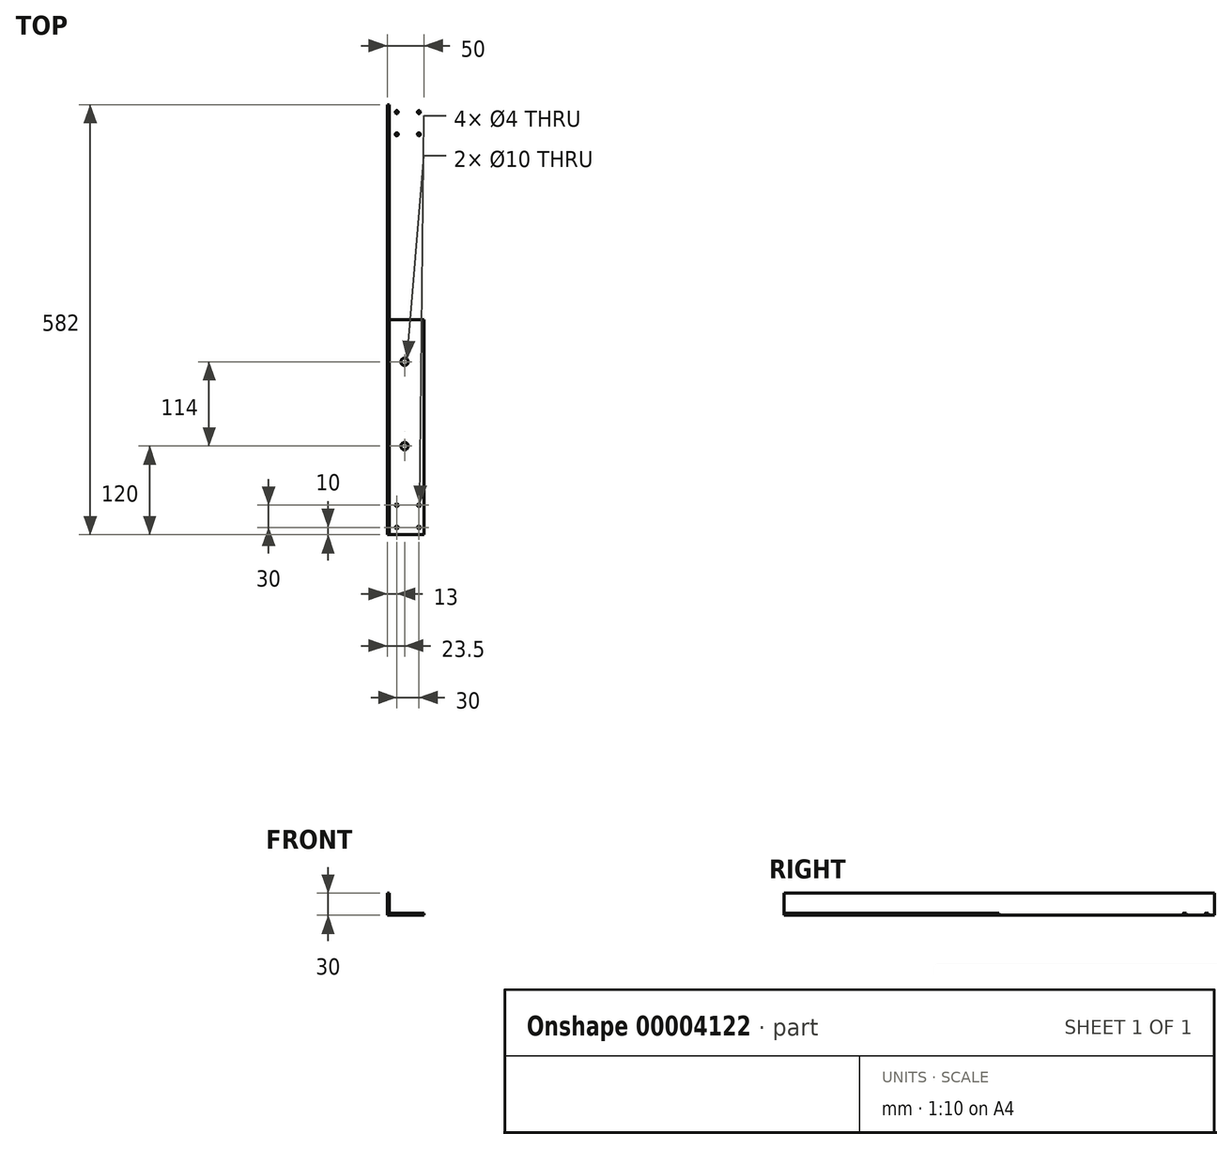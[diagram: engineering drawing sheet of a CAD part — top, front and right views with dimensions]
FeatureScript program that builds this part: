
annotation { "Feature Type Name" : "Feature", "Feature Type Description" : "" }
export const myFeature = defineFeature(function(context is Context, id is Id, definition is map)
    precondition{}
    {
        {
            var Q0;
            Q0=qCreatedBy(makeId("Front.planeOp"),FACE);
            var sketch = newSketch(context, id + "F0", { "sketchPlane" : qUnion([Q0])});
            skLineSegment(sketch, "E0", {"start": v(0, 0) * mm, "end": v(0, 30) * mm});
            skLineSegment(sketch, "E1", {"start": v(0, 30) * mm, "end": v(3, 30) * mm});
            skLineSegment(sketch, "E2", {"start": v(3, 30) * mm, "end": v(3, 3) * mm});
            skLineSegment(sketch, "E3", {"start": v(3, 3) * mm, "end": v(50, 3) * mm});
            skLineSegment(sketch, "E4", {"start": v(50, 3) * mm, "end": v(50, 0) * mm});
            skLineSegment(sketch, "E5", {"start": v(50, 0) * mm, "end": v(0, 0) * mm});
            skSolve(sketch);
        }
        {
            var Q0;
            Q0=makeQuery(id+"F0.imprint","IMPRINT",FACE,{"disambiguationData":[TD([[makeQuery(id+"F0.imprint","IMPRINT",EDGE,{"derivedFrom":sQuery(id+"F0.wireOp",EDGE,"E0")}),-1.0]])]});
            extrude(context, id + "F1", {"entities" : qUnion([Q0]), "depth" : 582 * mm});
        }
        {
            var Q0;
            Q0=makeQuery(id+"F1.opExtrude","SWEPT_FACE",FACE,{"disambiguationData":[OSD([sQuery(id+"F0.wireOp",EDGE,"E3")])]});
            var sketch = newSketch(context, id + "F2", { "sketchPlane" : qUnion([Q0])});
            skLineSegment(sketch, "E6", {"start": v(23.5, -582) * mm, "end": v(23.5, 0) * mm});
            skCircle(sketch, "E7", {"center": v(23.5, -462) * mm, "radius": 5 * mm});
            skCircle(sketch, "E8.0.1.0", {"center": v(23.5, -348) * mm, "radius": 5 * mm});
            skCircle(sketch, "E8.0.2.0", {"center": v(23.5, -234) * mm, "radius": 5 * mm});
            skCircle(sketch, "E8.0.3.0", {"center": v(23.5, -120) * mm, "radius": 5 * mm});
            skLineSegment(sketch, "E8.direction1", {"start": v(23.5, -462) * mm, "end": v(47.5, -462) * mm, "construction": true});
            skLineSegment(sketch, "E8.direction2", {"start": v(23.5, -462) * mm, "end": v(23.5, -348) * mm, "construction": true});
            skSolve(sketch);
        }
        {
            var Q0;
            {var subQ0=sQuery(id+"F2.wireOp",EDGE,"E7");var subQ1=sQuery(id+"F2.wireOp",EDGE,"E6");var subQ3=makeQuery(id+"F2.imprint","INTERSECT",VERTEX,{"disambiguationData":[OD(0.0)],"derivedFrom":[subQ1,subQ0]});var subQ4=sQuery(id+"F2.wireOp",EDGE,"E8.0.1.0");var subQ6=makeQuery(id+"F2.imprint","INTERSECT",VERTEX,{"disambiguationData":[OD(0.0)],"derivedFrom":[subQ1,subQ4]});var subQ7=sQuery(id+"F2.wireOp",EDGE,"E8.0.2.0");var subQ9=makeQuery(id+"F2.imprint","INTERSECT",VERTEX,{"disambiguationData":[OD(0.0)],"derivedFrom":[subQ1,subQ7]});var subQ10=sQuery(id+"F2.wireOp",EDGE,"E8.0.3.0");var subQ12=makeQuery(id+"F2.imprint","INTERSECT",VERTEX,{"disambiguationData":[OD(0.0)],"derivedFrom":[subQ1,subQ10]});Q0=qUnion([makeQuery(id+"F2.imprint","IMPRINT",FACE,{"disambiguationData":[TD([[makeQuery(id+"F2.imprint","IMPRINT",EDGE,{"disambiguationData":[TD([[subQ3,-1.0]])],"derivedFrom":subQ1}),1.0]])]}),makeQuery(id+"F2.imprint","IMPRINT",FACE,{"disambiguationData":[TD([[makeQuery(id+"F2.imprint","IMPRINT",EDGE,{"disambiguationData":[TD([[subQ6,-1.0]])],"derivedFrom":subQ1}),1.0]])]}),makeQuery(id+"F2.imprint","IMPRINT",FACE,{"disambiguationData":[TD([[makeQuery(id+"F2.imprint","IMPRINT",EDGE,{"disambiguationData":[TD([[subQ9,-1.0]])],"derivedFrom":subQ1}),1.0]])]}),makeQuery(id+"F2.imprint","IMPRINT",FACE,{"disambiguationData":[TD([[makeQuery(id+"F2.imprint","IMPRINT",EDGE,{"disambiguationData":[TD([[subQ12,-1.0]])],"derivedFrom":subQ1}),1.0]])]})]);}
            var Q1;
            {var subQ0=sQuery(id+"F2.wireOp",EDGE,"E7");var subQ1=sQuery(id+"F2.wireOp",EDGE,"E6");var subQ3=makeQuery(id+"F2.imprint","INTERSECT",VERTEX,{"disambiguationData":[OD(0.0)],"derivedFrom":[subQ1,subQ0]});var subQ4=sQuery(id+"F2.wireOp",EDGE,"E8.0.1.0");var subQ6=makeQuery(id+"F2.imprint","INTERSECT",VERTEX,{"disambiguationData":[OD(0.0)],"derivedFrom":[subQ1,subQ4]});var subQ7=sQuery(id+"F2.wireOp",EDGE,"E8.0.2.0");var subQ9=makeQuery(id+"F2.imprint","INTERSECT",VERTEX,{"disambiguationData":[OD(0.0)],"derivedFrom":[subQ1,subQ7]});var subQ10=sQuery(id+"F2.wireOp",EDGE,"E8.0.3.0");var subQ12=makeQuery(id+"F2.imprint","INTERSECT",VERTEX,{"disambiguationData":[OD(0.0)],"derivedFrom":[subQ1,subQ10]});Q1=qUnion([makeQuery(id+"F2.imprint","IMPRINT",FACE,{"disambiguationData":[TD([[makeQuery(id+"F2.imprint","IMPRINT",EDGE,{"disambiguationData":[TD([[subQ3,-1.0]])],"derivedFrom":subQ1}),-1.0]])]}),makeQuery(id+"F2.imprint","IMPRINT",FACE,{"disambiguationData":[TD([[makeQuery(id+"F2.imprint","IMPRINT",EDGE,{"disambiguationData":[TD([[subQ6,-1.0]])],"derivedFrom":subQ1}),-1.0]])]}),makeQuery(id+"F2.imprint","IMPRINT",FACE,{"disambiguationData":[TD([[makeQuery(id+"F2.imprint","IMPRINT",EDGE,{"disambiguationData":[TD([[subQ9,-1.0]])],"derivedFrom":subQ1}),-1.0]])]}),makeQuery(id+"F2.imprint","IMPRINT",FACE,{"disambiguationData":[TD([[makeQuery(id+"F2.imprint","IMPRINT",EDGE,{"disambiguationData":[TD([[subQ12,-1.0]])],"derivedFrom":subQ1}),-1.0]])]})]);}
            var Q2;
            {var subQ0=sQuery(id+"F2.wireOp",EDGE,"E7");var subQ1=sQuery(id+"F2.wireOp",EDGE,"E6");var subQ3=makeQuery(id+"F2.imprint","INTERSECT",VERTEX,{"disambiguationData":[OD(0.0)],"derivedFrom":[subQ1,subQ0]});var subQ4=sQuery(id+"F2.wireOp",EDGE,"E8.0.1.0");var subQ6=makeQuery(id+"F2.imprint","INTERSECT",VERTEX,{"disambiguationData":[OD(0.0)],"derivedFrom":[subQ1,subQ4]});var subQ7=sQuery(id+"F2.wireOp",EDGE,"E8.0.2.0");var subQ9=makeQuery(id+"F2.imprint","INTERSECT",VERTEX,{"disambiguationData":[OD(0.0)],"derivedFrom":[subQ1,subQ7]});var subQ10=sQuery(id+"F2.wireOp",EDGE,"E8.0.3.0");var subQ12=makeQuery(id+"F2.imprint","INTERSECT",VERTEX,{"disambiguationData":[OD(0.0)],"derivedFrom":[subQ1,subQ10]});Q2=qUnion([makeQuery(id+"F2.imprint","IMPRINT",FACE,{"disambiguationData":[TD([[makeQuery(id+"F2.imprint","IMPRINT",EDGE,{"disambiguationData":[TD([[subQ3,-1.0]])],"derivedFrom":subQ1}),-1.0]])]}),makeQuery(id+"F2.imprint","IMPRINT",FACE,{"disambiguationData":[TD([[makeQuery(id+"F2.imprint","IMPRINT",EDGE,{"disambiguationData":[TD([[subQ6,-1.0]])],"derivedFrom":subQ1}),-1.0]])]}),makeQuery(id+"F2.imprint","IMPRINT",FACE,{"disambiguationData":[TD([[makeQuery(id+"F2.imprint","IMPRINT",EDGE,{"disambiguationData":[TD([[subQ9,-1.0]])],"derivedFrom":subQ1}),-1.0]])]}),makeQuery(id+"F2.imprint","IMPRINT",FACE,{"disambiguationData":[TD([[makeQuery(id+"F2.imprint","IMPRINT",EDGE,{"disambiguationData":[TD([[subQ12,-1.0]])],"derivedFrom":subQ1}),-1.0]])]})]);}
            var Q3;
            {var subQ0=sQuery(id+"F2.wireOp",EDGE,"E7");var subQ1=sQuery(id+"F2.wireOp",EDGE,"E6");var subQ3=makeQuery(id+"F2.imprint","INTERSECT",VERTEX,{"disambiguationData":[OD(0.0)],"derivedFrom":[subQ1,subQ0]});var subQ4=sQuery(id+"F2.wireOp",EDGE,"E8.0.1.0");var subQ6=makeQuery(id+"F2.imprint","INTERSECT",VERTEX,{"disambiguationData":[OD(0.0)],"derivedFrom":[subQ1,subQ4]});var subQ7=sQuery(id+"F2.wireOp",EDGE,"E8.0.2.0");var subQ9=makeQuery(id+"F2.imprint","INTERSECT",VERTEX,{"disambiguationData":[OD(0.0)],"derivedFrom":[subQ1,subQ7]});var subQ10=sQuery(id+"F2.wireOp",EDGE,"E8.0.3.0");var subQ12=makeQuery(id+"F2.imprint","INTERSECT",VERTEX,{"disambiguationData":[OD(0.0)],"derivedFrom":[subQ1,subQ10]});Q3=qUnion([makeQuery(id+"F2.imprint","IMPRINT",FACE,{"disambiguationData":[TD([[makeQuery(id+"F2.imprint","IMPRINT",EDGE,{"disambiguationData":[TD([[subQ3,-1.0]])],"derivedFrom":subQ1}),1.0]])]}),makeQuery(id+"F2.imprint","IMPRINT",FACE,{"disambiguationData":[TD([[makeQuery(id+"F2.imprint","IMPRINT",EDGE,{"disambiguationData":[TD([[subQ6,-1.0]])],"derivedFrom":subQ1}),1.0]])]}),makeQuery(id+"F2.imprint","IMPRINT",FACE,{"disambiguationData":[TD([[makeQuery(id+"F2.imprint","IMPRINT",EDGE,{"disambiguationData":[TD([[subQ9,-1.0]])],"derivedFrom":subQ1}),1.0]])]}),makeQuery(id+"F2.imprint","IMPRINT",FACE,{"disambiguationData":[TD([[makeQuery(id+"F2.imprint","IMPRINT",EDGE,{"disambiguationData":[TD([[subQ12,-1.0]])],"derivedFrom":subQ1}),1.0]])]})]);}
            var Q4;
            {var subQ0=sQuery(id+"F2.wireOp",EDGE,"E8.0.3.0");var subQ1=sQuery(id+"F2.wireOp",EDGE,"E6");var subQ3=makeQuery(id+"F2.imprint","INTERSECT",VERTEX,{"disambiguationData":[OD(0.0)],"derivedFrom":[subQ1,subQ0]});Q4=makeQuery(id+"F2.imprint","IMPRINT",FACE,{"disambiguationData":[TD([[makeQuery(id+"F2.imprint","IMPRINT",EDGE,{"disambiguationData":[TD([[subQ3,-1.0]])],"derivedFrom":subQ1}),1.0]])]});}
            var Q5;
            {var subQ0=sQuery(id+"F2.wireOp",EDGE,"E8.0.3.0");var subQ1=sQuery(id+"F2.wireOp",EDGE,"E6");var subQ3=makeQuery(id+"F2.imprint","INTERSECT",VERTEX,{"disambiguationData":[OD(0.0)],"derivedFrom":[subQ1,subQ0]});Q5=makeQuery(id+"F2.imprint","IMPRINT",FACE,{"disambiguationData":[TD([[makeQuery(id+"F2.imprint","IMPRINT",EDGE,{"disambiguationData":[TD([[subQ3,-1.0]])],"derivedFrom":subQ1}),-1.0]])]});}
            var Q6;
            {var subQ0=sQuery(id+"F2.wireOp",EDGE,"E8.0.2.0");var subQ1=sQuery(id+"F2.wireOp",EDGE,"E6");var subQ3=makeQuery(id+"F2.imprint","INTERSECT",VERTEX,{"disambiguationData":[OD(0.0)],"derivedFrom":[subQ1,subQ0]});Q6=makeQuery(id+"F2.imprint","IMPRINT",FACE,{"disambiguationData":[TD([[makeQuery(id+"F2.imprint","IMPRINT",EDGE,{"disambiguationData":[TD([[subQ3,-1.0]])],"derivedFrom":subQ1}),-1.0]])]});}
            var Q7;
            {var subQ0=sQuery(id+"F2.wireOp",EDGE,"E8.0.2.0");var subQ1=sQuery(id+"F2.wireOp",EDGE,"E6");var subQ3=makeQuery(id+"F2.imprint","INTERSECT",VERTEX,{"disambiguationData":[OD(0.0)],"derivedFrom":[subQ1,subQ0]});Q7=makeQuery(id+"F2.imprint","IMPRINT",FACE,{"disambiguationData":[TD([[makeQuery(id+"F2.imprint","IMPRINT",EDGE,{"disambiguationData":[TD([[subQ3,-1.0]])],"derivedFrom":subQ1}),1.0]])]});}
            var Q8;
            {var subQ0=sQuery(id+"F2.wireOp",EDGE,"E8.0.1.0");var subQ1=sQuery(id+"F2.wireOp",EDGE,"E6");var subQ3=makeQuery(id+"F2.imprint","INTERSECT",VERTEX,{"disambiguationData":[OD(0.0)],"derivedFrom":[subQ1,subQ0]});Q8=makeQuery(id+"F2.imprint","IMPRINT",FACE,{"disambiguationData":[TD([[makeQuery(id+"F2.imprint","IMPRINT",EDGE,{"disambiguationData":[TD([[subQ3,-1.0]])],"derivedFrom":subQ1}),1.0]])]});}
            var Q9;
            {var subQ0=sQuery(id+"F2.wireOp",EDGE,"E8.0.1.0");var subQ1=sQuery(id+"F2.wireOp",EDGE,"E6");var subQ3=makeQuery(id+"F2.imprint","INTERSECT",VERTEX,{"disambiguationData":[OD(0.0)],"derivedFrom":[subQ1,subQ0]});Q9=makeQuery(id+"F2.imprint","IMPRINT",FACE,{"disambiguationData":[TD([[makeQuery(id+"F2.imprint","IMPRINT",EDGE,{"disambiguationData":[TD([[subQ3,-1.0]])],"derivedFrom":subQ1}),-1.0]])]});}
            var Q10;
            {var subQ0=sQuery(id+"F2.wireOp",EDGE,"E7");var subQ1=sQuery(id+"F2.wireOp",EDGE,"E6");var subQ3=makeQuery(id+"F2.imprint","INTERSECT",VERTEX,{"disambiguationData":[OD(0.0)],"derivedFrom":[subQ1,subQ0]});Q10=makeQuery(id+"F2.imprint","IMPRINT",FACE,{"disambiguationData":[TD([[makeQuery(id+"F2.imprint","IMPRINT",EDGE,{"disambiguationData":[TD([[subQ3,-1.0]])],"derivedFrom":subQ1}),1.0]])]});}
            var Q11;
            {var subQ0=sQuery(id+"F2.wireOp",EDGE,"E7");var subQ1=sQuery(id+"F2.wireOp",EDGE,"E6");var subQ3=makeQuery(id+"F2.imprint","INTERSECT",VERTEX,{"disambiguationData":[OD(0.0)],"derivedFrom":[subQ1,subQ0]});Q11=makeQuery(id+"F2.imprint","IMPRINT",FACE,{"disambiguationData":[TD([[makeQuery(id+"F2.imprint","IMPRINT",EDGE,{"disambiguationData":[TD([[subQ3,-1.0]])],"derivedFrom":subQ1}),-1.0]])]});}
            extrude(context, id + "F3", {"entities" : qUnion([Q0, Q1, Q2, Q3, Q4, Q5, Q6, Q7, Q8, Q9, Q10, Q11]), "operationType" : NewBodyOperationType.REMOVE, "oppositeDirection" : true, "depth" : 25 * mm});
        }
        {
            var Q0;
            Q0=makeQuery(id+"F1.opExtrude","SWEPT_FACE",FACE,{"disambiguationData":[OSD([sQuery(id+"F0.wireOp",EDGE,"E3")])]});
            var sketch = newSketch(context, id + "F4", { "sketchPlane" : qUnion([Q0])});
            skLineSegment(sketch, "E9.bottom", {"start": v(13, -542) * mm, "end": v(43, -542) * mm});
            skLineSegment(sketch, "E9.top", {"start": v(13, -572) * mm, "end": v(43, -572) * mm});
            skLineSegment(sketch, "E9.left", {"start": v(13, -542) * mm, "end": v(13, -572) * mm});
            skLineSegment(sketch, "E9.right", {"start": v(43, -542) * mm, "end": v(43, -572) * mm});
            skCircle(sketch, "E10", {"center": v(43, -542) * mm, "radius": 2 * mm});
            skCircle(sketch, "E11", {"center": v(13, -542) * mm, "radius": 2 * mm});
            skCircle(sketch, "E12", {"center": v(13, -572) * mm, "radius": 2 * mm});
            skCircle(sketch, "E13", {"center": v(43, -572) * mm, "radius": 2 * mm});
            skLineSegment(sketch, "E14", {"start": v(3, -291) * mm, "end": v(162.3, -291) * mm});
            skCircle(sketch, "E15.0.MirrorC", {"center": v(13, -40) * mm, "radius": 2 * mm});
            skCircle(sketch, "E16.0.MirrorC", {"center": v(43, -10) * mm, "radius": 2 * mm});
            skCircle(sketch, "E17.0.MirrorC", {"center": v(13, -10) * mm, "radius": 2 * mm});
            skCircle(sketch, "E18.0.MirrorC", {"center": v(43, -40) * mm, "radius": 2 * mm});
            skSolve(sketch);
        }
        {
            var Q0;
            {var subQ1=sQuery(id+"F4.wireOp",EDGE,"E9.left");var subQ3=sQuery(id+"F4.wireOp",EDGE,"E9.bottom");var subQ5=makeQuery(id+"F4.imprint","INTERSECT",VERTEX,{"derivedFrom":[subQ3,subQ1]});Q0=makeQuery(id+"F4.imprint","IMPRINT",FACE,{"disambiguationData":[TD([[makeQuery(id+"F4.imprint","IMPRINT",EDGE,{"disambiguationData":[TD([[subQ5,-1.0]])],"derivedFrom":subQ3}),1.0]])]});}
            var Q1;
            {var subQ1=sQuery(id+"F4.wireOp",EDGE,"E9.left");var subQ3=sQuery(id+"F4.wireOp",EDGE,"E9.top");var subQ5=makeQuery(id+"F4.imprint","INTERSECT",VERTEX,{"derivedFrom":[subQ3,subQ1]});Q1=makeQuery(id+"F4.imprint","IMPRINT",FACE,{"disambiguationData":[TD([[makeQuery(id+"F4.imprint","IMPRINT",EDGE,{"disambiguationData":[TD([[subQ5,-1.0]])],"derivedFrom":subQ3}),-1.0]])]});}
            var Q2;
            {var subQ1=sQuery(id+"F4.wireOp",EDGE,"E9.left");var subQ3=sQuery(id+"F4.wireOp",EDGE,"E9.top");var subQ5=makeQuery(id+"F4.imprint","INTERSECT",VERTEX,{"derivedFrom":[subQ3,subQ1]});Q2=makeQuery(id+"F4.imprint","IMPRINT",FACE,{"disambiguationData":[TD([[makeQuery(id+"F4.imprint","IMPRINT",EDGE,{"disambiguationData":[TD([[subQ5,-1.0]])],"derivedFrom":subQ3}),1.0]])]});}
            var Q3;
            {var subQ0=sQuery(id+"F4.wireOp",EDGE,"E9.right");var subQ3=sQuery(id+"F4.wireOp",EDGE,"E9.top");var subQ4=makeQuery(id+"F4.imprint","INTERSECT",VERTEX,{"derivedFrom":[subQ3,subQ0]});Q3=makeQuery(id+"F4.imprint","IMPRINT",FACE,{"disambiguationData":[TD([[makeQuery(id+"F4.imprint","IMPRINT",EDGE,{"disambiguationData":[TD([[subQ4,1.0]])],"derivedFrom":subQ3}),1.0]])]});}
            var Q4;
            {var subQ1=sQuery(id+"F4.wireOp",EDGE,"E9.right");var subQ3=sQuery(id+"F4.wireOp",EDGE,"E9.top");var subQ5=makeQuery(id+"F4.imprint","INTERSECT",VERTEX,{"derivedFrom":[subQ3,subQ1]});Q4=makeQuery(id+"F4.imprint","IMPRINT",FACE,{"disambiguationData":[TD([[makeQuery(id+"F4.imprint","IMPRINT",EDGE,{"disambiguationData":[TD([[subQ5,1.0]])],"derivedFrom":subQ3}),-1.0]])]});}
            var Q5;
            {var subQ0=sQuery(id+"F4.wireOp",EDGE,"E9.right");var subQ3=sQuery(id+"F4.wireOp",EDGE,"E9.bottom");var subQ4=makeQuery(id+"F4.imprint","INTERSECT",VERTEX,{"derivedFrom":[subQ3,subQ0]});Q5=makeQuery(id+"F4.imprint","IMPRINT",FACE,{"disambiguationData":[TD([[makeQuery(id+"F4.imprint","IMPRINT",EDGE,{"disambiguationData":[TD([[subQ4,1.0]])],"derivedFrom":subQ3}),-1.0]])]});}
            var Q6;
            {var subQ1=sQuery(id+"F4.wireOp",EDGE,"E9.right");var subQ3=sQuery(id+"F4.wireOp",EDGE,"E9.bottom");var subQ5=makeQuery(id+"F4.imprint","INTERSECT",VERTEX,{"derivedFrom":[subQ3,subQ1]});Q6=makeQuery(id+"F4.imprint","IMPRINT",FACE,{"disambiguationData":[TD([[makeQuery(id+"F4.imprint","IMPRINT",EDGE,{"disambiguationData":[TD([[subQ5,1.0]])],"derivedFrom":subQ3}),1.0]])]});}
            var Q7;
            {var subQ1=sQuery(id+"F4.wireOp",EDGE,"E9.left");var subQ3=sQuery(id+"F4.wireOp",EDGE,"E9.bottom");var subQ5=makeQuery(id+"F4.imprint","INTERSECT",VERTEX,{"derivedFrom":[subQ3,subQ1]});Q7=makeQuery(id+"F4.imprint","IMPRINT",FACE,{"disambiguationData":[TD([[makeQuery(id+"F4.imprint","IMPRINT",EDGE,{"disambiguationData":[TD([[subQ5,-1.0]])],"derivedFrom":subQ3}),-1.0]])]});}
            var Q8;
            Q8=makeQuery(id+"F4.imprint","IMPRINT",FACE,{"disambiguationData":[TD([[makeQuery(id+"F4.imprint","IMPRINT",EDGE,{"derivedFrom":sQuery(id+"F4.wireOp",EDGE,"E15.0.MirrorC")}),-1.0]])]});
            var Q9;
            Q9=makeQuery(id+"F4.imprint","IMPRINT",FACE,{"disambiguationData":[TD([[makeQuery(id+"F4.imprint","IMPRINT",EDGE,{"derivedFrom":sQuery(id+"F4.wireOp",EDGE,"E18.0.MirrorC")}),-1.0]])]});
            var Q10;
            Q10=makeQuery(id+"F4.imprint","IMPRINT",FACE,{"disambiguationData":[TD([[makeQuery(id+"F4.imprint","IMPRINT",EDGE,{"derivedFrom":sQuery(id+"F4.wireOp",EDGE,"E16.0.MirrorC")}),-1.0]])]});
            var Q11;
            Q11=makeQuery(id+"F4.imprint","IMPRINT",FACE,{"disambiguationData":[TD([[makeQuery(id+"F4.imprint","IMPRINT",EDGE,{"derivedFrom":sQuery(id+"F4.wireOp",EDGE,"E17.0.MirrorC")}),-1.0]])]});
            extrude(context, id + "F5", {"entities" : qUnion([Q0, Q1, Q2, Q3, Q4, Q5, Q6, Q7, Q8, Q9, Q10, Q11]), "operationType" : NewBodyOperationType.REMOVE, "oppositeDirection" : true, "depth" : 25 * mm});
        }
    });
